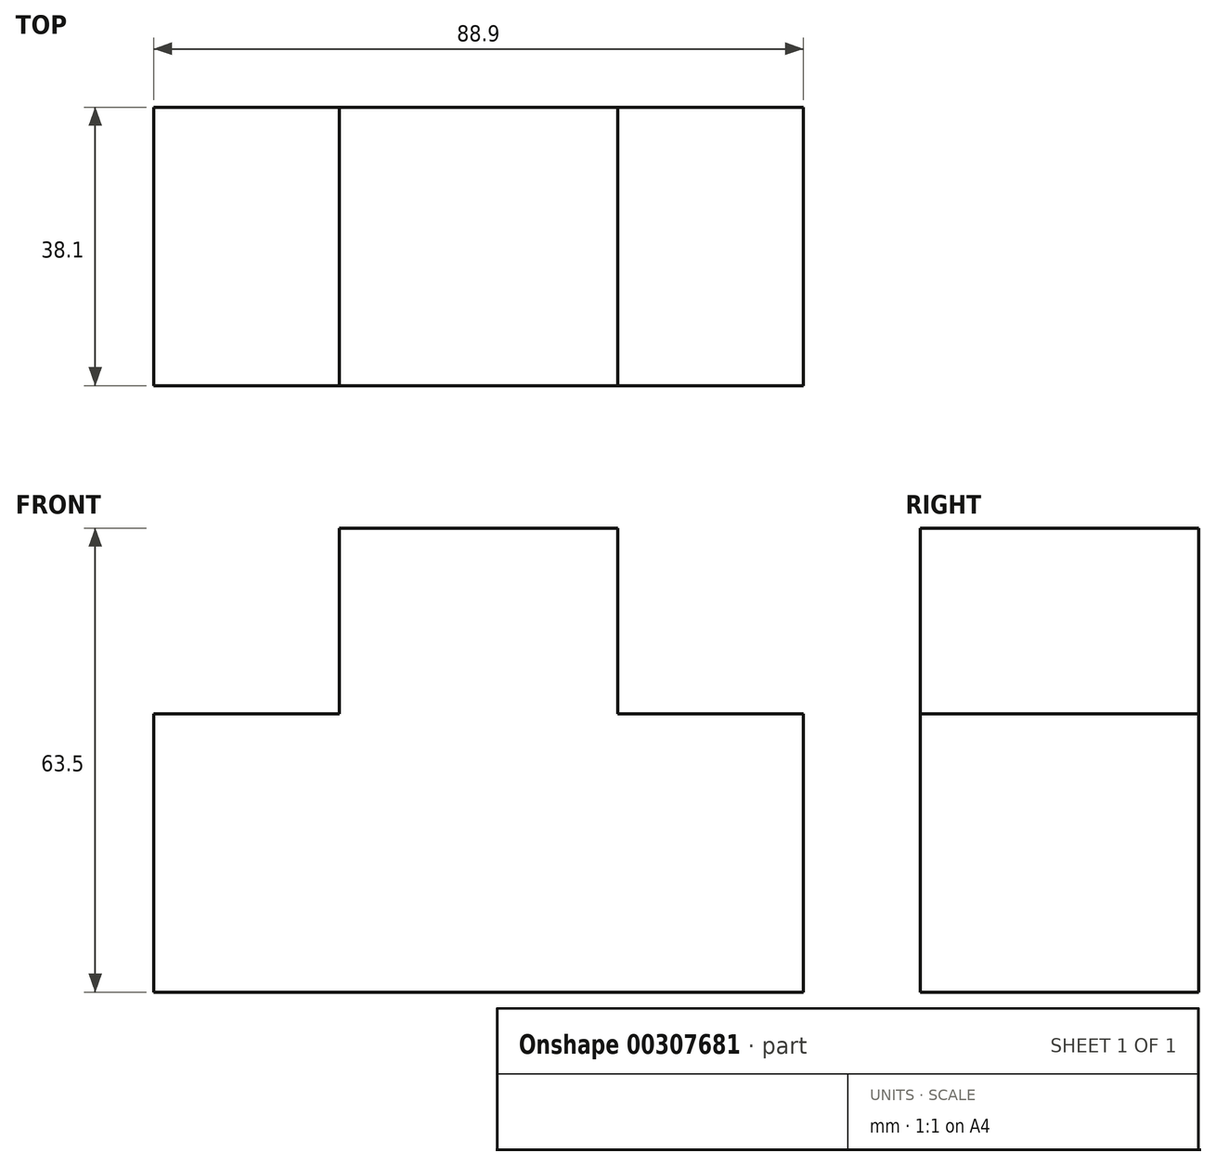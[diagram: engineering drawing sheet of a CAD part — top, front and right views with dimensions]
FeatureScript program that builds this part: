
annotation { "Feature Type Name" : "Feature", "Feature Type Description" : "" }
export const myFeature = defineFeature(function(context is Context, id is Id, definition is map)
    precondition{}
    {
        {
            var Q0;
            Q0=qCreatedBy(makeId("Front.planeOp"),FACE);
            var sketch = newSketch(context, id + "F0", { "sketchPlane" : qUnion([Q0])});
            skLineSegment(sketch, "E0", {"start": v(-50.52, -48.28) * mm, "end": v(38.38, -48.28) * mm});
            skLineSegment(sketch, "E1", {"start": v(38.38, -48.28) * mm, "end": v(38.38, -10.18) * mm});
            skLineSegment(sketch, "E2", {"start": v(38.38, -10.18) * mm, "end": v(12.98, -10.18) * mm});
            skLineSegment(sketch, "E3", {"start": v(12.98, -10.18) * mm, "end": v(12.98, 15.22) * mm});
            skLineSegment(sketch, "E4", {"start": v(12.98, 15.22) * mm, "end": v(-25.12, 15.22) * mm});
            skLineSegment(sketch, "E5", {"start": v(-25.12, 15.22) * mm, "end": v(-25.12, -10.18) * mm});
            skLineSegment(sketch, "E6", {"start": v(-25.12, -10.18) * mm, "end": v(-50.52, -10.18) * mm});
            skLineSegment(sketch, "E7", {"start": v(-50.52, -10.18) * mm, "end": v(-50.52, -48.28) * mm});
            skSolve(sketch);
        }
        {
            var Q0;
            Q0=makeQuery(id+"F0.imprint","IMPRINT",FACE,{"disambiguationData":[TD([[makeQuery(id+"F0.imprint","IMPRINT",EDGE,{"derivedFrom":sQuery(id+"F0.wireOp",EDGE,"E0")}),1.0]])]});
            extrude(context, id + "F1", {"entities" : qUnion([Q0]), "depth" : 38.1 * mm});
        }
    });
